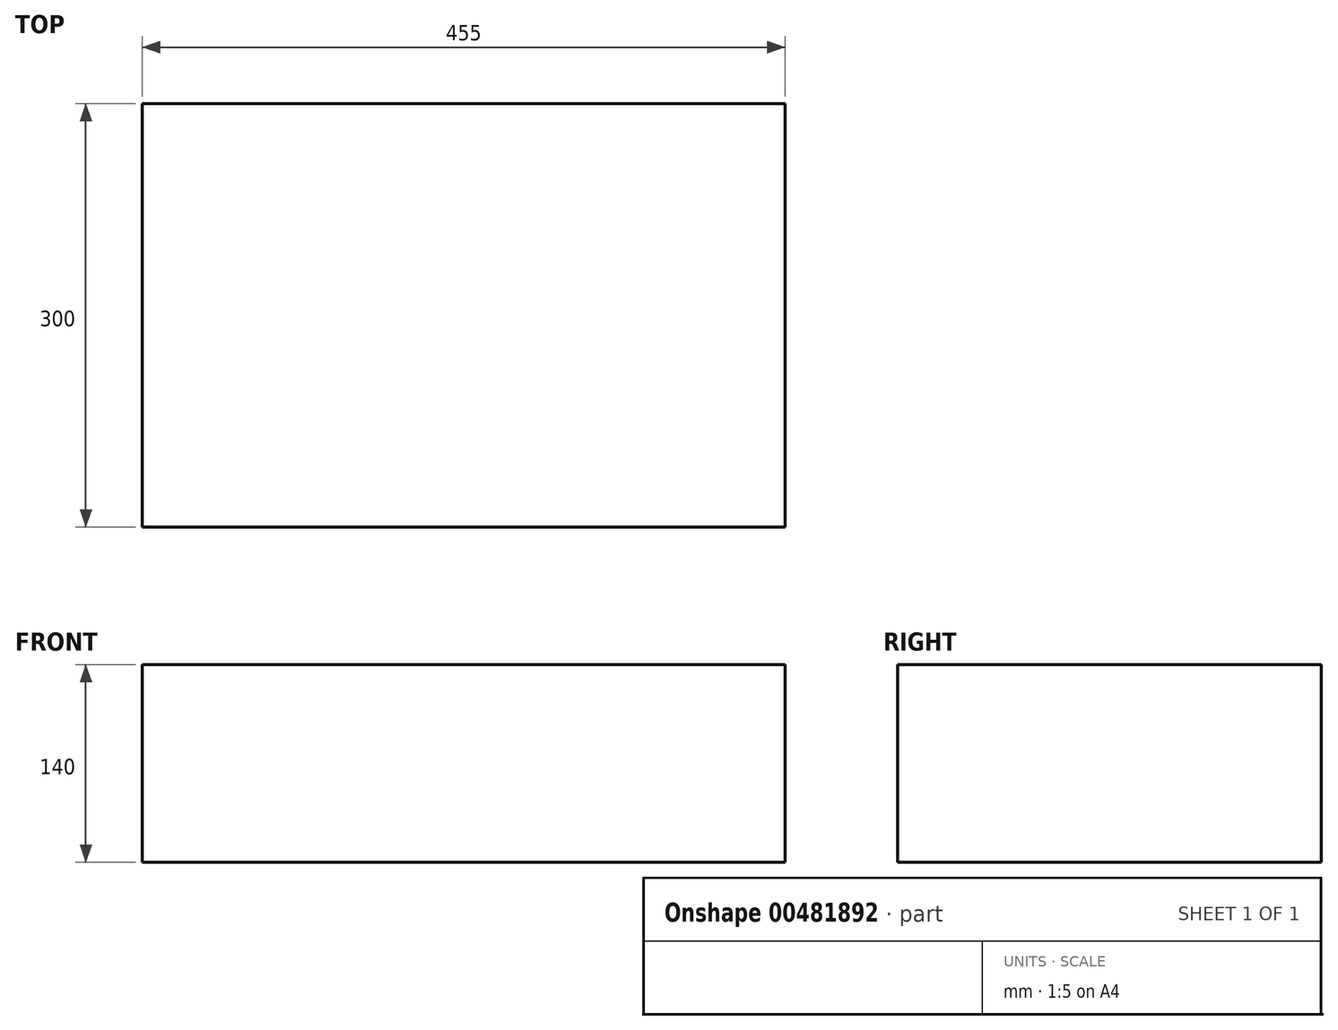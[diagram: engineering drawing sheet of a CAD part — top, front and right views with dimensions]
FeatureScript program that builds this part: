
annotation { "Feature Type Name" : "Feature", "Feature Type Description" : "" }
export const myFeature = defineFeature(function(context is Context, id is Id, definition is map)
    precondition{}
    {
        {
            var Q0;
            Q0=qCreatedBy(makeId("Right.planeOp"),FACE);
            var sketch = newSketch(context, id + "F0", { "sketchPlane" : qUnion([Q0])});
            skLineSegment(sketch, "E0.bottom", {"start": v(0, 0) * mm, "end": v(300, 0) * mm});
            skLineSegment(sketch, "E0.top", {"start": v(0, 140) * mm, "end": v(300, 140) * mm});
            skLineSegment(sketch, "E0.left", {"start": v(0, 0) * mm, "end": v(0, 140) * mm});
            skLineSegment(sketch, "E0.right", {"start": v(300, 0) * mm, "end": v(300, 140) * mm});
            skSolve(sketch);
        }
        {
            var Q0;
            Q0 = qSketchRegion(id + "F0", true);
            extrude(context, id + "F1", {"entities" : qUnion([Q0]), "depth" : 455 * mm});
        }
    });
